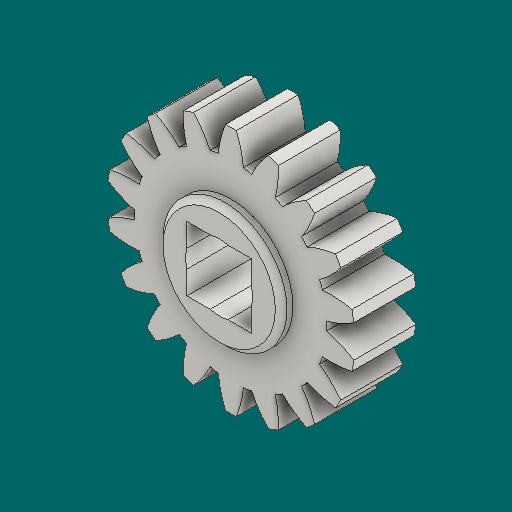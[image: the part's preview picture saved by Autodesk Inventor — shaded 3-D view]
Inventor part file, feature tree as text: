
AUTODESK INVENTOR PART (.ipt)
format: ipt  version: 2023.1 (Build 271208000, 208)  size: 329,216 bytes
history: native  units: in
note: dims shown in document units (in); Inventor stores cm internally (conversion verified against a paired STEP export)
features: other x12, sketch x4, plane x3
ambient origin geometry x8: Origin, YZ Plane, XZ Plane, XY Plane, X Axis, Y Axis, Z Axis, Center Point
bodies: Solid1 (feature_tree)
feature tree (19):
  other  "Spur Gear1"
  other  "Solid1::Spur Gear1"
  other  "TaggingFeature1"
  sketch  "Sketch1"  dims[d0=0.3937in]
  sketch  "Sketch2"  dims[d9=0.0in]
  sketch  "Sketch3"  dims[d14=0.0in]
  sketch  "Sketch4"  dims[d15=0.9in d16=0.0in d17=0.0in d18=0.0in d19=0.9in]
  plane  "XZ Plane_1"
  plane  "Work Plane2"
  plane  "Work Plane3"
  other  "Srf1"
  other  "Srf1::Derived"
  other  "Start plane iMate"
  other  "Distance iMate"
  other  "Position iMate"
  other  "Mesh iMate"
  other  "Axis iMate"
  other  "Mesh iMate2"
  other  "Align iMate"
